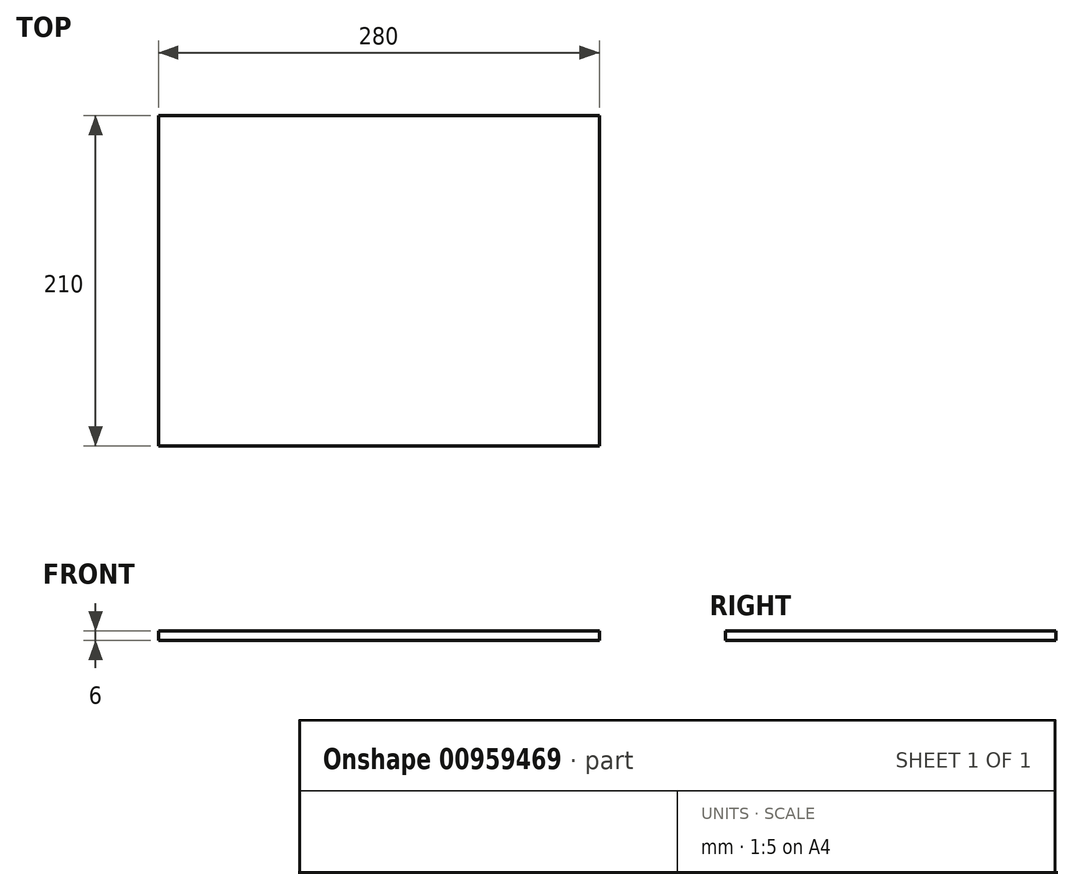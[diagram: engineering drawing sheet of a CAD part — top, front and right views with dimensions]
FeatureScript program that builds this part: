
annotation { "Feature Type Name" : "Feature", "Feature Type Description" : "" }
export const myFeature = defineFeature(function(context is Context, id is Id, definition is map)
    precondition{}
    {
        {
            var Q0;
            Q0=qCreatedBy(makeId("Top.planeOp"),FACE);
            var sketch = newSketch(context, id + "F0", { "sketchPlane" : qUnion([Q0])});
            skLineSegment(sketch, "E0.bottom", {"start": v(-140, 105) * mm, "end": v(140, 105) * mm});
            skLineSegment(sketch, "E0.top", {"start": v(-140, -105) * mm, "end": v(140, -105) * mm});
            skLineSegment(sketch, "E0.left", {"start": v(-140, 105) * mm, "end": v(-140, -105) * mm});
            skLineSegment(sketch, "E0.right", {"start": v(140, 105) * mm, "end": v(140, -105) * mm});
            skSolve(sketch);
        }
        {
            var Q0;
            Q0 = qSketchRegion(id + "F0", true);
            extrude(context, id + "F1", {"entities" : qUnion([Q0]), "depth" : 6 * mm, "offsetDistance" : 25 * mm});
        }
    });
